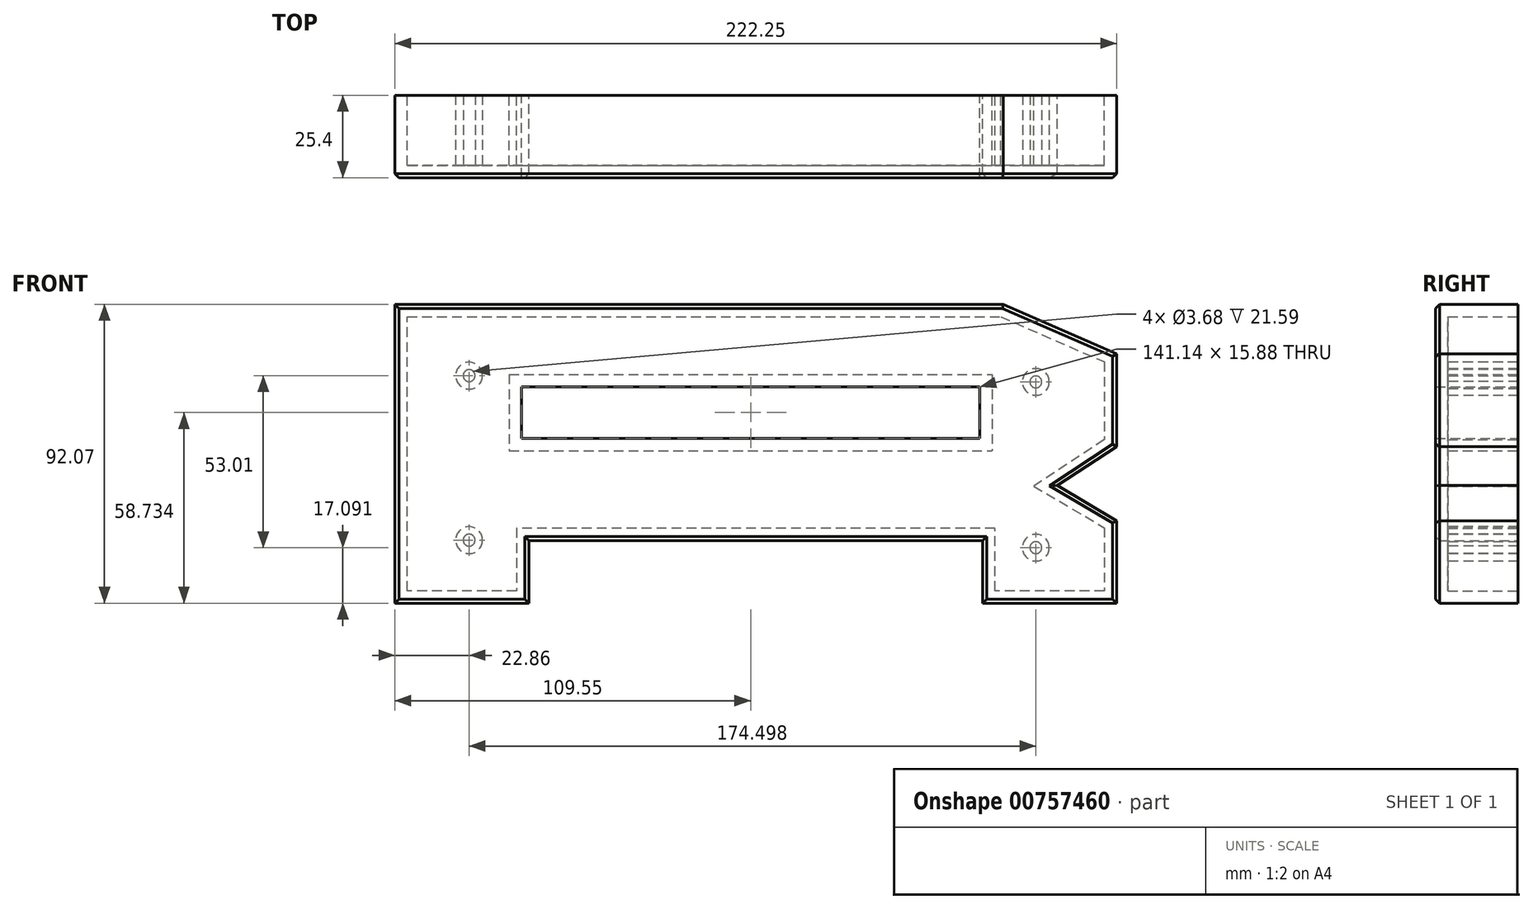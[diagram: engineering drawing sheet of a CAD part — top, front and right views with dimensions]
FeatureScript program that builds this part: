
annotation { "Feature Type Name" : "Feature", "Feature Type Description" : "" }
export const myFeature = defineFeature(function(context is Context, id is Id, definition is map)
    precondition{}
    {
        {
            var Q0;
            Q0=qCreatedBy(makeId("Front.planeOp"),FACE);
            var sketch = newSketch(context, id + "F0", { "sketchPlane" : qUnion([Q0])});
            skLineSegment(sketch, "E0", {"start": v(-71.64, 43.8) * mm, "end": v(115.69, 43.8) * mm});
            skLineSegment(sketch, "E1", {"start": v(115.69, 43.8) * mm, "end": v(150.61, 28.57) * mm});
            skLineSegment(sketch, "E2", {"start": v(150.61, 28.57) * mm, "end": v(150.61, 0) * mm});
            skLineSegment(sketch, "E3", {"start": v(150.61, 0) * mm, "end": v(132.27, -12.02) * mm});
            skLineSegment(sketch, "E4", {"start": v(132.27, -12.02) * mm, "end": v(150.61, -22.87) * mm});
            skLineSegment(sketch, "E5", {"start": v(150.61, -22.87) * mm, "end": v(150.61, -48.27) * mm});
            skLineSegment(sketch, "E6", {"start": v(150.61, -48.27) * mm, "end": v(109.34, -48.27) * mm});
            skLineSegment(sketch, "E7", {"start": v(109.34, -48.27) * mm, "end": v(109.34, -28.97) * mm});
            skLineSegment(sketch, "E8", {"start": v(109.34, -28.97) * mm, "end": v(-30.36, -28.97) * mm});
            skLineSegment(sketch, "E9", {"start": v(-30.36, -28.97) * mm, "end": v(-30.36, -48.27) * mm});
            skLineSegment(sketch, "E10", {"start": v(-30.36, -48.27) * mm, "end": v(-71.64, -48.27) * mm});
            skLineSegment(sketch, "E11", {"start": v(-71.64, -48.27) * mm, "end": v(-71.64, 43.8) * mm});
            skLineSegment(sketch, "E12.bottom", {"start": v(-32.66, 18.4) * mm, "end": v(108.48, 18.4) * mm});
            skLineSegment(sketch, "E12.top", {"start": v(-32.66, 2.53) * mm, "end": v(108.48, 2.53) * mm});
            skLineSegment(sketch, "E12.left", {"start": v(-32.66, 18.4) * mm, "end": v(-32.66, 2.53) * mm});
            skLineSegment(sketch, "E12.right", {"start": v(108.48, 18.4) * mm, "end": v(108.48, 2.53) * mm});
            skSolve(sketch);
        }
        {
            var Q0;
            Q0 = qSketchRegion(id + "F0", true);
            extrude(context, id + "F1", {"entities" : qUnion([Q0]), "depth" : 25.4 * mm, "offsetDistance" : 25.4 * mm});
        }
        {
            var Q0;
            Q0=makeQuery(id+"F1.opExtrude","CAP_EDGE",EDGE,{"disambiguationData":[OSD([sQuery(id+"F0.wireOp",EDGE,"E11")])],"isStart":false});
            var Q1;
            Q1=makeQuery(id+"F1.opExtrude","CAP_EDGE",EDGE,{"disambiguationData":[OSD([sQuery(id+"F0.wireOp",EDGE,"E0")])],"isStart":false});
            var Q2;
            Q2=makeQuery(id+"F1.opExtrude","CAP_EDGE",EDGE,{"disambiguationData":[OSD([sQuery(id+"F0.wireOp",EDGE,"MCfNfoF9-p8M5-l3RX-WTCi-vgsPNKxJpFSk")])],"isStart":false});
            var Q3;
            Q3=makeQuery(id+"F1.opExtrude","CAP_EDGE",EDGE,{"disambiguationData":[OSD([sQuery(id+"F0.wireOp",EDGE,"W2JI7Zt6-RgL1-u0UN-PGmf-Yhlp3doEdCLf")])],"isStart":false});
            var Q4;
            Q4=makeQuery(id+"F1.opExtrude","CAP_EDGE",EDGE,{"disambiguationData":[OSD([sQuery(id+"F0.wireOp",EDGE,"whyWtqe0-U2Xs-VF5G-yfXT-ZjwdRDDCOACX")])],"isStart":false});
            var Q5;
            Q5=makeQuery(id+"F1.opExtrude","CAP_EDGE",EDGE,{"disambiguationData":[OSD([sQuery(id+"F0.wireOp",EDGE,"U7EugQMz-Pq8V-SVv4-LMp5-7rIeizR3xOU0")])],"isStart":false});
            var Q6;
            Q6=makeQuery(id+"F1.opExtrude","CAP_EDGE",EDGE,{"disambiguationData":[OSD([sQuery(id+"F0.wireOp",EDGE,"E1")])],"isStart":false});
            var Q7;
            Q7=makeQuery(id+"F1.opExtrude","CAP_EDGE",EDGE,{"disambiguationData":[OSD([sQuery(id+"F0.wireOp",EDGE,"E2")])],"isStart":false});
            var Q8;
            Q8=makeQuery(id+"F1.opExtrude","CAP_EDGE",EDGE,{"disambiguationData":[OSD([sQuery(id+"F0.wireOp",EDGE,"E3")])],"isStart":false});
            var Q9;
            Q9=makeQuery(id+"F1.opExtrude","CAP_EDGE",EDGE,{"disambiguationData":[OSD([sQuery(id+"F0.wireOp",EDGE,"E4")])],"isStart":false});
            var Q10;
            Q10=makeQuery(id+"F1.opExtrude","CAP_EDGE",EDGE,{"disambiguationData":[OSD([sQuery(id+"F0.wireOp",EDGE,"E5")])],"isStart":false});
            var Q11;
            Q11=makeQuery(id+"F1.opExtrude","CAP_EDGE",EDGE,{"disambiguationData":[OSD([sQuery(id+"F0.wireOp",EDGE,"E6")])],"isStart":false});
            var Q12;
            Q12=makeQuery(id+"F1.opExtrude","CAP_EDGE",EDGE,{"disambiguationData":[OSD([sQuery(id+"F0.wireOp",EDGE,"E7")])],"isStart":false});
            var Q13;
            Q13=makeQuery(id+"F1.opExtrude","CAP_EDGE",EDGE,{"disambiguationData":[OSD([sQuery(id+"F0.wireOp",EDGE,"E8")])],"isStart":false});
            var Q14;
            Q14=makeQuery(id+"F1.opExtrude","CAP_EDGE",EDGE,{"disambiguationData":[OSD([sQuery(id+"F0.wireOp",EDGE,"E9")])],"isStart":false});
            var Q15;
            Q15=makeQuery(id+"F1.opExtrude","CAP_EDGE",EDGE,{"disambiguationData":[OSD([sQuery(id+"F0.wireOp",EDGE,"E10")])],"isStart":false});
            chamfer(context, id + "F2", {"entities" : qUnion([Q0, Q1, Q2, Q3, Q4, Q5, Q6, Q7, Q8, Q9, Q10, Q11, Q12, Q13, Q14, Q15]), "width" : 1.27 * mm, "tangentPropagation" : true});
        }
        {
            var Q0;
            Q0=makeQuery(id+"F1.opExtrude","CAP_FACE",FACE,{"disambiguationData":[OSD([sQuery(id+"F0.wireOp",EDGE,"E0"),sQuery(id+"F0.wireOp",EDGE,"E1"),sQuery(id+"F0.wireOp",EDGE,"E2"),sQuery(id+"F0.wireOp",EDGE,"E3"),sQuery(id+"F0.wireOp",EDGE,"E4"),sQuery(id+"F0.wireOp",EDGE,"E5"),sQuery(id+"F0.wireOp",EDGE,"E6"),sQuery(id+"F0.wireOp",EDGE,"E7"),sQuery(id+"F0.wireOp",EDGE,"E8"),sQuery(id+"F0.wireOp",EDGE,"E9"),sQuery(id+"F0.wireOp",EDGE,"E10"),sQuery(id+"F0.wireOp",EDGE,"E11"),sQuery(id+"F0.wireOp",EDGE,"W2JI7Zt6-RgL1-u0UN-PGmf-Yhlp3doEdCLf"),sQuery(id+"F0.wireOp",EDGE,"whyWtqe0-U2Xs-VF5G-yfXT-ZjwdRDDCOACX"),sQuery(id+"F0.wireOp",EDGE,"U7EugQMz-Pq8V-SVv4-LMp5-7rIeizR3xOU0"),sQuery(id+"F0.wireOp",EDGE,"MCfNfoF9-p8M5-l3RX-WTCi-vgsPNKxJpFSk")])],"isStart":true});
            shell(context, id + "F3", {"entities" : qUnion([Q0]), "thickness" : 3.8 * mm});
        }
        {
            var Q0;
            {var subQ0=sQuery(id+"F0.wireOp",EDGE,"E12.right");var subQ1=sQuery(id+"F0.wireOp",EDGE,"E12.left");var subQ2=sQuery(id+"F0.wireOp",EDGE,"E12.top");var subQ3=sQuery(id+"F0.wireOp",EDGE,"E12.bottom");var subQ4=sQuery(id+"F0.wireOp",EDGE,"E11");var subQ5=sQuery(id+"F0.wireOp",EDGE,"E10");var subQ6=sQuery(id+"F0.wireOp",EDGE,"E9");var subQ7=sQuery(id+"F0.wireOp",EDGE,"E8");var subQ8=sQuery(id+"F0.wireOp",EDGE,"E7");var subQ9=sQuery(id+"F0.wireOp",EDGE,"E6");var subQ10=sQuery(id+"F0.wireOp",EDGE,"E5");var subQ11=sQuery(id+"F0.wireOp",EDGE,"E4");var subQ12=sQuery(id+"F0.wireOp",EDGE,"E3");var subQ13=sQuery(id+"F0.wireOp",EDGE,"E2");var subQ14=sQuery(id+"F0.wireOp",EDGE,"E1");var subQ15=sQuery(id+"F0.wireOp",EDGE,"E0");Q0=makeQuery(id+"F3.opShell","OFFSET_FACE",FACE,{"disambiguationData":[OSD([subQ15,subQ14,subQ13,subQ12,subQ11,subQ10,subQ9,subQ8,subQ7,subQ6,subQ5,subQ4,subQ3,subQ2,subQ1,subQ0]),TDD([makeQuery(id+"F1.opExtrude","CAP_FACE",FACE,{"disambiguationData":[OSD([subQ15,subQ14,subQ13,subQ12,subQ11,subQ10,subQ9,subQ8,subQ7,subQ6,subQ5,subQ4,subQ3,subQ2,subQ1,subQ0])],"isStart":false})])]});}
            var sketch = newSketch(context, id + "F4", { "sketchPlane" : qUnion([Q0])});
            skCircle(sketch, "E13", {"center": v(48.78, 21.83) * mm, "radius": 4.13 * mm});
            skCircle(sketch, "E14", {"center": v(48.78, 21.83) * mm, "radius": 1.84 * mm});
            skCircle(sketch, "E15", {"center": v(48.78, -28.84) * mm, "radius": 4.13 * mm});
            skCircle(sketch, "E16", {"center": v(48.78, -28.84) * mm, "radius": 1.84 * mm});
            skCircle(sketch, "E17", {"center": v(-125.72, 19.9) * mm, "radius": 4.13 * mm});
            skCircle(sketch, "E18", {"center": v(-125.72, 19.9) * mm, "radius": 1.84 * mm});
            skCircle(sketch, "E19", {"center": v(-125.72, -31.18) * mm, "radius": 4.13 * mm});
            skCircle(sketch, "E20", {"center": v(-125.72, -31.18) * mm, "radius": 1.84 * mm});
            skSolve(sketch);
        }
        {
            var Q0;
            Q0 = qSketchRegion(id + "F4", true);
            var Q1;
            Q1=makeQuery(id+"F1.opExtrude","CAP_FACE",FACE,{"disambiguationData":[OSD([sQuery(id+"F0.wireOp",EDGE,"E0"),sQuery(id+"F0.wireOp",EDGE,"E1"),sQuery(id+"F0.wireOp",EDGE,"E2"),sQuery(id+"F0.wireOp",EDGE,"E3"),sQuery(id+"F0.wireOp",EDGE,"E4"),sQuery(id+"F0.wireOp",EDGE,"E5"),sQuery(id+"F0.wireOp",EDGE,"E6"),sQuery(id+"F0.wireOp",EDGE,"E7"),sQuery(id+"F0.wireOp",EDGE,"E8"),sQuery(id+"F0.wireOp",EDGE,"E9"),sQuery(id+"F0.wireOp",EDGE,"E10"),sQuery(id+"F0.wireOp",EDGE,"E11"),sQuery(id+"F0.wireOp",EDGE,"E12.bottom"),sQuery(id+"F0.wireOp",EDGE,"E12.top"),sQuery(id+"F0.wireOp",EDGE,"E12.left"),sQuery(id+"F0.wireOp",EDGE,"E12.right")])],"isStart":true});
            extrude(context, id + "F5", {"entities" : qUnion([Q0]), "operationType" : NewBodyOperationType.ADD, "endBound" : BoundingType.UP_TO_SURFACE, "depth" : 25.4 * mm, "endBoundEntityFace" : qUnion([Q1]), "offsetDistance" : 25.4 * mm});
        }
    });
